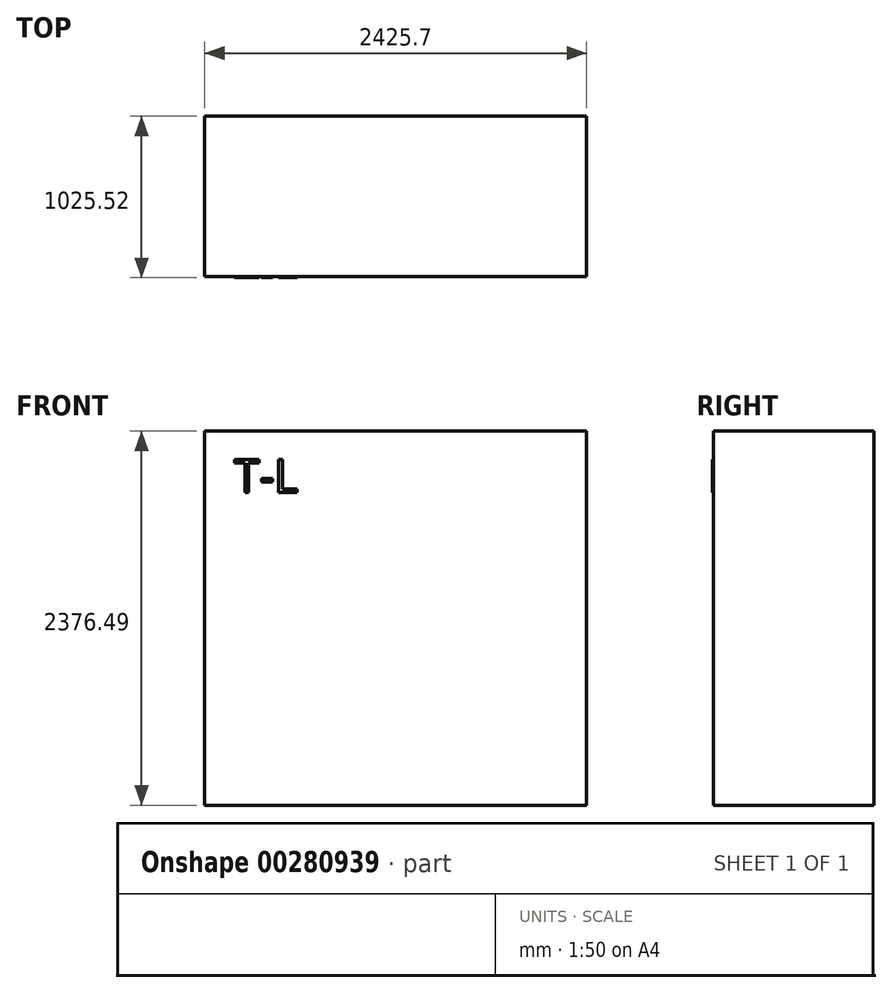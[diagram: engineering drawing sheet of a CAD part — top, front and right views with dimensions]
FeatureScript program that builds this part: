
annotation { "Feature Type Name" : "Feature", "Feature Type Description" : "" }
export const myFeature = defineFeature(function(context is Context, id is Id, definition is map)
    precondition{}
    {
        {
            var Q0;
            Q0=qCreatedBy(makeId("Top.planeOp"),FACE);
            var sketch = newSketch(context, id + "F0", { "sketchPlane" : qUnion([Q0])});
            skLineSegment(sketch, "E0.bottom", {"start": v(0, 0) * mm, "end": v(2425.7, 0) * mm});
            skLineSegment(sketch, "E0.top", {"start": v(0, 1019.18) * mm, "end": v(2425.7, 1019.18) * mm});
            skLineSegment(sketch, "E0.left", {"start": v(0, 0) * mm, "end": v(0, 1019.18) * mm});
            skLineSegment(sketch, "E0.right", {"start": v(2425.7, 0) * mm, "end": v(2425.7, 1019.18) * mm});
            skSolve(sketch);
        }
        {
            var Q0;
            Q0=makeQuery(id+"F0.imprint","IMPRINT",FACE,{"disambiguationData":[TD([[makeQuery(id+"F0.imprint","IMPRINT",EDGE,{"derivedFrom":sQuery(id+"F0.wireOp",EDGE,"E0.bottom")}),1.0]])]});
            extrude(context, id + "F1", {"entities" : qUnion([Q0]), "depth" : 2376.49 * mm});
        }
        {
            var Q0;
            Q0=makeQuery(id+"F1.opExtrude","SWEPT_FACE",FACE,{"disambiguationData":[OSD([sQuery(id+"F0.wireOp",EDGE,"E0.bottom")])]});
            var sketch = newSketch(context, id + "F2", { "sketchPlane" : qUnion([Q0])});
            skText(sketch, "E1", { "text": "T-L", "fontName": "OpenSans-Regular.ttf"});
            const initialGuessF2  = {"E1": [0.18801, 1.98771, 1, 0, 0.20919]};
            skSetInitialGuess(sketch, initialGuessF2);
            skSolve(sketch);
        }
        {
            var Q0;
            Q0 = qSketchRegion(id + "F2", true);
            extrude(context, id + "F3", {"entities" : qUnion([Q0]), "operationType" : NewBodyOperationType.ADD, "depth" : 6.35 * mm});
        }
    });
